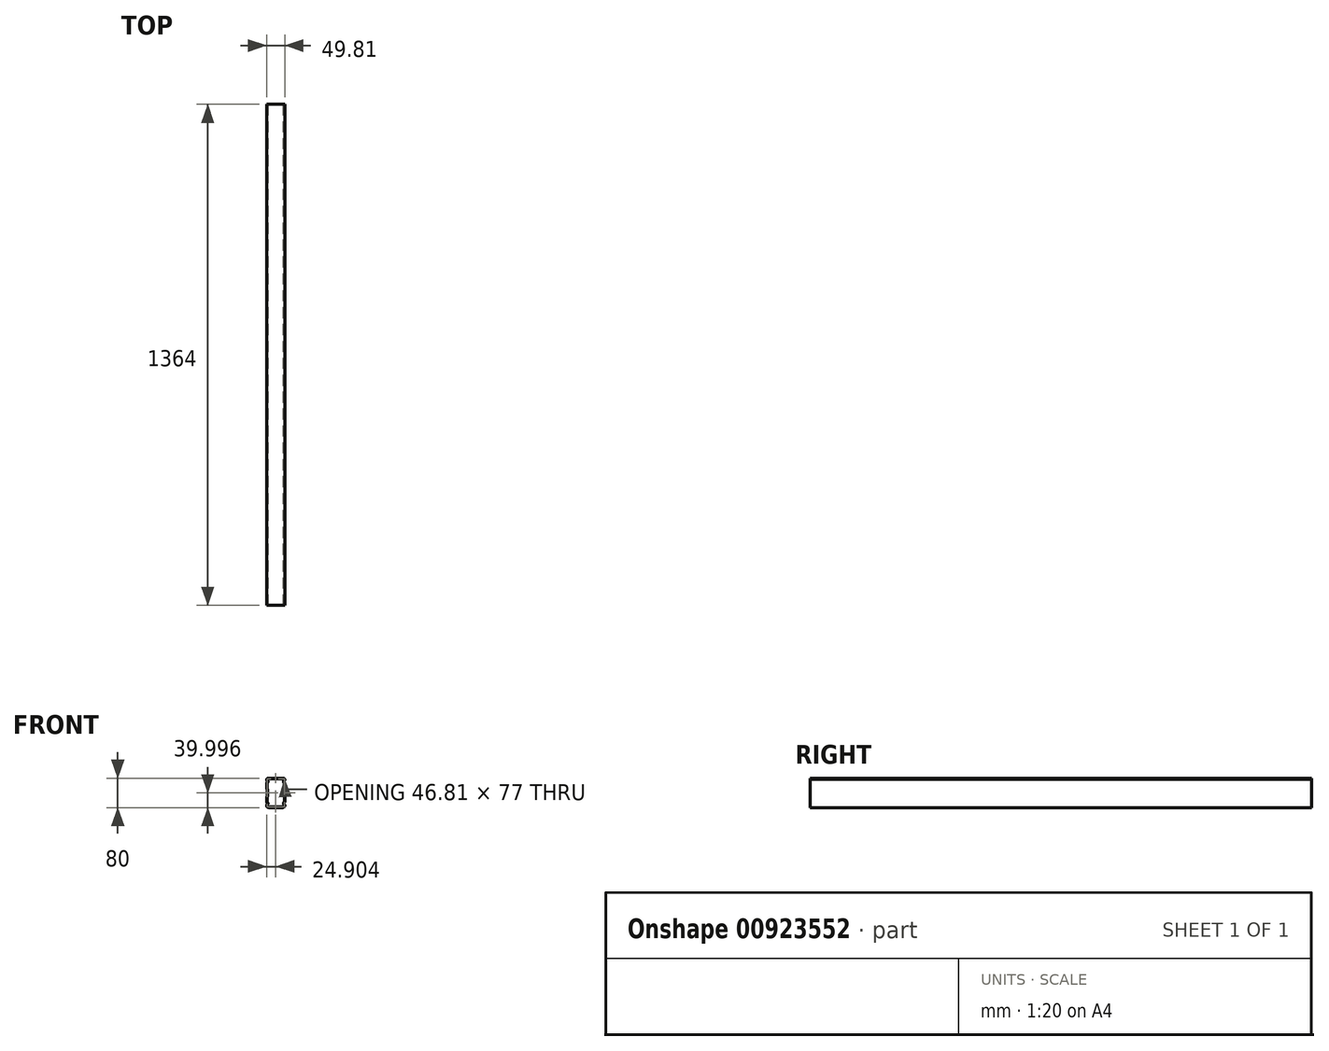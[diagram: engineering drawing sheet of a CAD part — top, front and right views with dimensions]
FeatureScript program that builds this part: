
annotation { "Feature Type Name" : "Feature", "Feature Type Description" : "" }
export const myFeature = defineFeature(function(context is Context, id is Id, definition is map)
    precondition{}
    {
        {
            var Q0;
            Q0=qCreatedBy(makeId("Front.planeOp"),FACE);
            var sketch = newSketch(context, id + "F0", { "sketchPlane" : qUnion([Q0])});
            skLineSegment(sketch, "E0.bottom", {"start": v(-66.37, 65.7) * mm, "end": v(-26.18, 65.7) * mm});
            skLineSegment(sketch, "E0.top", {"start": v(-66.18, -14.3) * mm, "end": v(-26.18, -14.3) * mm});
            skArc(sketch, "E1.filletArc", {"start": v(-66.37, 65.7) * mm, "mid": v(-69.38, 64.7) * mm, "end": v(-71.18, 62.07) * mm});
            skArc(sketch, "E2.filletArc", {"start": v(-71.18, -9.3) * mm, "mid": v(-69.72, -12.83) * mm, "end": v(-66.18, -14.3) * mm});
            skArc(sketch, "E3", {"start": v(-69.34, -4.86) * mm, "mid": v(-70.7, -6.9) * mm, "end": v(-71.18, -9.3) * mm});
            skArc(sketch, "E4", {"start": v(-68.78, -3.08) * mm, "mid": v(-69.4, -1.3) * mm, "end": v(-70.56, 0.2) * mm});
            skArc(sketch, "E5.filletArc", {"start": v(-69.34, -4.86) * mm, "mid": v(-68.84, -4.04) * mm, "end": v(-68.78, -3.08) * mm});
            skLineSegment(sketch, "E6", {"start": v(-71.18, 1.64) * mm, "end": v(-71.18, 14.24) * mm});
            skLineSegment(sketch, "E7", {"start": v(-71.18, 15.7) * mm, "end": v(-71.18, 15.7) * mm});
            skLineSegment(sketch, "E8", {"start": v(-69.18, 17.7) * mm, "end": v(-69.18, 33.7) * mm});
            skLineSegment(sketch, "E9", {"start": v(-71.18, 35.7) * mm, "end": v(-71.18, 35.7) * mm});
            skArc(sketch, "E10.filletArc", {"start": v(-70.18, 15.97) * mm, "mid": v(-69.45, 16.7) * mm, "end": v(-69.18, 17.7) * mm});
            skPoint(sketch, "E11.visualSharp", {"position": v(-71.18, 15.7) * mm});
            skArc(sketch, "E11.filletArc", {"start": v(-70.18, 15.97) * mm, "mid": v(-70.91, 15.24) * mm, "end": v(-71.18, 14.24) * mm});
            skArc(sketch, "E12.filletArc", {"start": v(-69.18, 33.7) * mm, "mid": v(-69.45, 34.7) * mm, "end": v(-70.18, 35.44) * mm});
            skPoint(sketch, "E13.visualSharp", {"position": v(-71.18, 35.7) * mm});
            skArc(sketch, "E13.filletArc", {"start": v(-71.18, 37.17) * mm, "mid": v(-70.91, 36.17) * mm, "end": v(-70.18, 35.44) * mm});
            skArc(sketch, "E14.filletArc", {"start": v(-71.18, 1.64) * mm, "mid": v(-71.02, 0.85) * mm, "end": v(-70.56, 0.2) * mm});
            skArc(sketch, "E15", {"start": v(-71.18, 62.07) * mm, "mid": v(-70.7, 59.68) * mm, "end": v(-69.35, 57.65) * mm});
            skArc(sketch, "E16", {"start": v(-70.57, 52.6) * mm, "mid": v(-69.44, 54.09) * mm, "end": v(-68.8, 55.85) * mm});
            skArc(sketch, "E17.filletArc", {"start": v(-68.8, 55.85) * mm, "mid": v(-68.85, 56.82) * mm, "end": v(-69.35, 57.65) * mm});
            skArc(sketch, "E18.filletArc", {"start": v(-70.57, 52.6) * mm, "mid": v(-71.02, 51.94) * mm, "end": v(-71.18, 51.16) * mm});
            skLineSegment(sketch, "E19", {"start": v(-71.18, 37.17) * mm, "end": v(-71.18, 51.16) * mm});
            skArc(sketch, "E20.MirrorCS", {"start": v(-21.37, 37.17) * mm, "mid": v(-21.64, 36.17) * mm, "end": v(-22.37, 35.44) * mm});
            skArc(sketch, "E21.MirrorCS", {"start": v(-23.37, 33.7) * mm, "mid": v(-23.1, 34.7) * mm, "end": v(-22.37, 35.44) * mm});
            skArc(sketch, "E22.MirrorCS", {"start": v(-22.37, 15.97) * mm, "mid": v(-23.1, 16.7) * mm, "end": v(-23.37, 17.7) * mm});
            skArc(sketch, "E23.MirrorCS", {"start": v(-22.37, 15.97) * mm, "mid": v(-21.64, 15.24) * mm, "end": v(-21.37, 14.24) * mm});
            skArc(sketch, "E24.MirrorCS", {"start": v(-21.98, 52.6) * mm, "mid": v(-21.53, 51.94) * mm, "end": v(-21.37, 51.16) * mm});
            skArc(sketch, "E25.MirrorCS", {"start": v(-23.22, -4.86) * mm, "mid": v(-23.71, -4.04) * mm, "end": v(-23.77, -3.08) * mm});
            skArc(sketch, "E26.MirrorCS", {"start": v(-21.37, 1.64) * mm, "mid": v(-21.53, 0.85) * mm, "end": v(-22, 0.2) * mm});
            skArc(sketch, "E27.MirrorCS", {"start": v(-23.75, 55.85) * mm, "mid": v(-23.7, 56.82) * mm, "end": v(-23.2, 57.65) * mm});
            skArc(sketch, "E28.MirrorCS", {"start": v(-21.98, 52.6) * mm, "mid": v(-23.11, 54.09) * mm, "end": v(-23.75, 55.85) * mm});
            skArc(sketch, "E29.MirrorCS", {"start": v(-23.77, -3.08) * mm, "mid": v(-23.14, -1.3) * mm, "end": v(-22, 0.2) * mm});
            skArc(sketch, "E30.MirrorCS", {"start": v(-21.37, 62.07) * mm, "mid": v(-21.85, 59.68) * mm, "end": v(-23.2, 57.65) * mm});
            skArc(sketch, "E31.MirrorCS", {"start": v(-23.22, -4.86) * mm, "mid": v(-21.85, -6.9) * mm, "end": v(-21.37, -9.3) * mm});
            skPoint(sketch, "E32.MirrorP", {"position": v(-21.37, 35.7) * mm});
            skArc(sketch, "E33.MirrorCS", {"start": v(-21.37, -9.3) * mm, "mid": v(-22.84, -12.83) * mm, "end": v(-26.37, -14.3) * mm});
            skArc(sketch, "E34.MirrorCS", {"start": v(-26.18, 65.7) * mm, "mid": v(-23.17, 64.7) * mm, "end": v(-21.37, 62.07) * mm});
            skPoint(sketch, "E35.MirrorP", {"position": v(-21.37, 52.07) * mm});
            skPoint(sketch, "E36.MirrorP", {"position": v(-23.37, 35.7) * mm});
            skLineSegment(sketch, "E37.MirrorCS", {"start": v(-21.37, 37.17) * mm, "end": v(-21.37, 51.16) * mm});
            skPoint(sketch, "E38.MirrorP", {"position": v(-23.87, 57.07) * mm});
            skLineSegment(sketch, "E39.MirrorCS", {"start": v(-21.37, 1.64) * mm, "end": v(-21.37, 14.24) * mm});
            skLineSegment(sketch, "E40.MirrorCS", {"start": v(-23.37, 17.7) * mm, "end": v(-23.37, 33.7) * mm});
            skSolve(sketch);
        }
        {
            var Q0;
            Q0=makeQuery(id+"F0.imprint","IMPRINT",FACE,{"disambiguationData":[TD([[makeQuery(id+"F0.imprint","IMPRINT",EDGE,{"derivedFrom":sQuery(id+"F0.wireOp",EDGE,"E0.bottom")}),-1.0]])]});
            extrude(context, id + "F1", {"entities" : qUnion([Q0]), "flatOperationType" : FlatOperationType.REMOVE, "depth" : 1364 * mm, "offsetDistance" : 25 * mm, "domain" : OperationDomain.MODEL});
        }
        {
            var Q0;
            Q0=makeQuery(id+"F1.opExtrude","CAP_FACE",FACE,{"disambiguationData":[OSD([sQuery(id+"F0.wireOp",EDGE,"E0.bottom"),sQuery(id+"F0.wireOp",EDGE,"E0.top"),sQuery(id+"F0.wireOp",EDGE,"E1.filletArc"),sQuery(id+"F0.wireOp",EDGE,"E2.filletArc"),sQuery(id+"F0.wireOp",EDGE,"E3"),sQuery(id+"F0.wireOp",EDGE,"E4"),sQuery(id+"F0.wireOp",EDGE,"E5.filletArc"),sQuery(id+"F0.wireOp",EDGE,"E6"),sQuery(id+"F0.wireOp",EDGE,"E8"),sQuery(id+"F0.wireOp",EDGE,"E10.filletArc"),sQuery(id+"F0.wireOp",EDGE,"E11.filletArc"),sQuery(id+"F0.wireOp",EDGE,"E12.filletArc"),sQuery(id+"F0.wireOp",EDGE,"E13.filletArc"),sQuery(id+"F0.wireOp",EDGE,"E14.filletArc"),sQuery(id+"F0.wireOp",EDGE,"E15"),sQuery(id+"F0.wireOp",EDGE,"E16"),sQuery(id+"F0.wireOp",EDGE,"E17.filletArc"),sQuery(id+"F0.wireOp",EDGE,"E18.filletArc"),sQuery(id+"F0.wireOp",EDGE,"E19"),sQuery(id+"F0.wireOp",EDGE,"E20.MirrorCS"),sQuery(id+"F0.wireOp",EDGE,"E21.MirrorCS"),sQuery(id+"F0.wireOp",EDGE,"E22.MirrorCS"),sQuery(id+"F0.wireOp",EDGE,"E23.MirrorCS"),sQuery(id+"F0.wireOp",EDGE,"E24.MirrorCS"),sQuery(id+"F0.wireOp",EDGE,"E25.MirrorCS"),sQuery(id+"F0.wireOp",EDGE,"E26.MirrorCS"),sQuery(id+"F0.wireOp",EDGE,"E27.MirrorCS"),sQuery(id+"F0.wireOp",EDGE,"E28.MirrorCS"),sQuery(id+"F0.wireOp",EDGE,"E29.MirrorCS"),sQuery(id+"F0.wireOp",EDGE,"E30.MirrorCS"),sQuery(id+"F0.wireOp",EDGE,"E31.MirrorCS"),sQuery(id+"F0.wireOp",EDGE,"E33.MirrorCS"),sQuery(id+"F0.wireOp",EDGE,"E34.MirrorCS"),sQuery(id+"F0.wireOp",EDGE,"E37.MirrorCS"),sQuery(id+"F0.wireOp",EDGE,"E39.MirrorCS"),sQuery(id+"F0.wireOp",EDGE,"E40.MirrorCS")])],"isStart":true});
            var Q1;
            Q1=makeQuery(id+"F1.opExtrude","CAP_FACE",FACE,{"disambiguationData":[OSD([sQuery(id+"F0.wireOp",EDGE,"E0.bottom"),sQuery(id+"F0.wireOp",EDGE,"E0.top"),sQuery(id+"F0.wireOp",EDGE,"E1.filletArc"),sQuery(id+"F0.wireOp",EDGE,"E2.filletArc"),sQuery(id+"F0.wireOp",EDGE,"E3"),sQuery(id+"F0.wireOp",EDGE,"E4"),sQuery(id+"F0.wireOp",EDGE,"E5.filletArc"),sQuery(id+"F0.wireOp",EDGE,"E6"),sQuery(id+"F0.wireOp",EDGE,"E8"),sQuery(id+"F0.wireOp",EDGE,"E10.filletArc"),sQuery(id+"F0.wireOp",EDGE,"E11.filletArc"),sQuery(id+"F0.wireOp",EDGE,"E12.filletArc"),sQuery(id+"F0.wireOp",EDGE,"E13.filletArc"),sQuery(id+"F0.wireOp",EDGE,"E14.filletArc"),sQuery(id+"F0.wireOp",EDGE,"E15"),sQuery(id+"F0.wireOp",EDGE,"E16"),sQuery(id+"F0.wireOp",EDGE,"E17.filletArc"),sQuery(id+"F0.wireOp",EDGE,"E18.filletArc"),sQuery(id+"F0.wireOp",EDGE,"E19"),sQuery(id+"F0.wireOp",EDGE,"E20.MirrorCS"),sQuery(id+"F0.wireOp",EDGE,"E21.MirrorCS"),sQuery(id+"F0.wireOp",EDGE,"E22.MirrorCS"),sQuery(id+"F0.wireOp",EDGE,"E23.MirrorCS"),sQuery(id+"F0.wireOp",EDGE,"E24.MirrorCS"),sQuery(id+"F0.wireOp",EDGE,"E25.MirrorCS"),sQuery(id+"F0.wireOp",EDGE,"E26.MirrorCS"),sQuery(id+"F0.wireOp",EDGE,"E27.MirrorCS"),sQuery(id+"F0.wireOp",EDGE,"E28.MirrorCS"),sQuery(id+"F0.wireOp",EDGE,"E29.MirrorCS"),sQuery(id+"F0.wireOp",EDGE,"E30.MirrorCS"),sQuery(id+"F0.wireOp",EDGE,"E31.MirrorCS"),sQuery(id+"F0.wireOp",EDGE,"E33.MirrorCS"),sQuery(id+"F0.wireOp",EDGE,"E34.MirrorCS"),sQuery(id+"F0.wireOp",EDGE,"E37.MirrorCS"),sQuery(id+"F0.wireOp",EDGE,"E39.MirrorCS"),sQuery(id+"F0.wireOp",EDGE,"E40.MirrorCS")])],"isStart":false});
            shell(context, id + "F2", {"entities" : qUnion([Q0, Q1]), "thickness" : 1.5 * mm});
        }
    });
